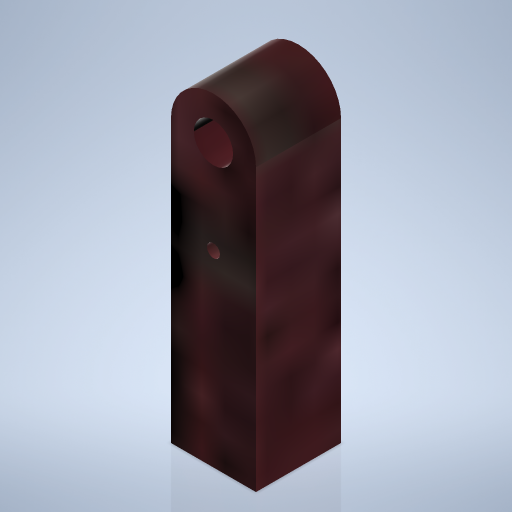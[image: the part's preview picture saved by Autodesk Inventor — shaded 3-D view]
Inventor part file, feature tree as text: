
AUTODESK INVENTOR PART (.ipt)
format: ipt  version: 2024 (Build 280153000, 153)  size: 294,400 bytes
history: native  units: mm
features: sketch x4, extrude x2, hole x2
ambient origin geometry x8: Origin, YZ Plane, XZ Plane, XY Plane, X Axis, Y Axis, Z Axis, Center Point
bodies: Volumenkörper1 (feature_tree)
feature tree (8):
  extrude  "Extrusion1"  Depth=43.0mm
  hole  "Bohrung1"  [1 undecoded]
  extrude  "Extrusion2"  Depth=7.0mm
  hole  "Bohrung2"  [1 undecoded]
  sketch  "Skizze1"  dims[d0=13.0mm d1=43.0mm]
  sketch  "Skizze2"  dims[d2=6.5mm d3=6.5mm]
  sketch  "Skizze3"  dims[d4=13.0mm d5=0.0mm]
  sketch  "Skizze4"  dims[d6=6.0mm d7=6.0mm d8=4.0mm d9=2.0mm d10=90.0deg d11=15.0mm d12=0.0mm d13=7.0mm d14=36.0mm d15=0.0mm d16=2.0mm d17=6.0mm d18=4.0mm d19=2.0mm d20=90.0deg d21=4.0mm d22=0.0mm d23=14.3mm]
note: 2 required parameter values undecoded (feature->parameter linkage not recoverable at this tier; creation-order binding heuristic only, values carry confidence <= 0.55)
